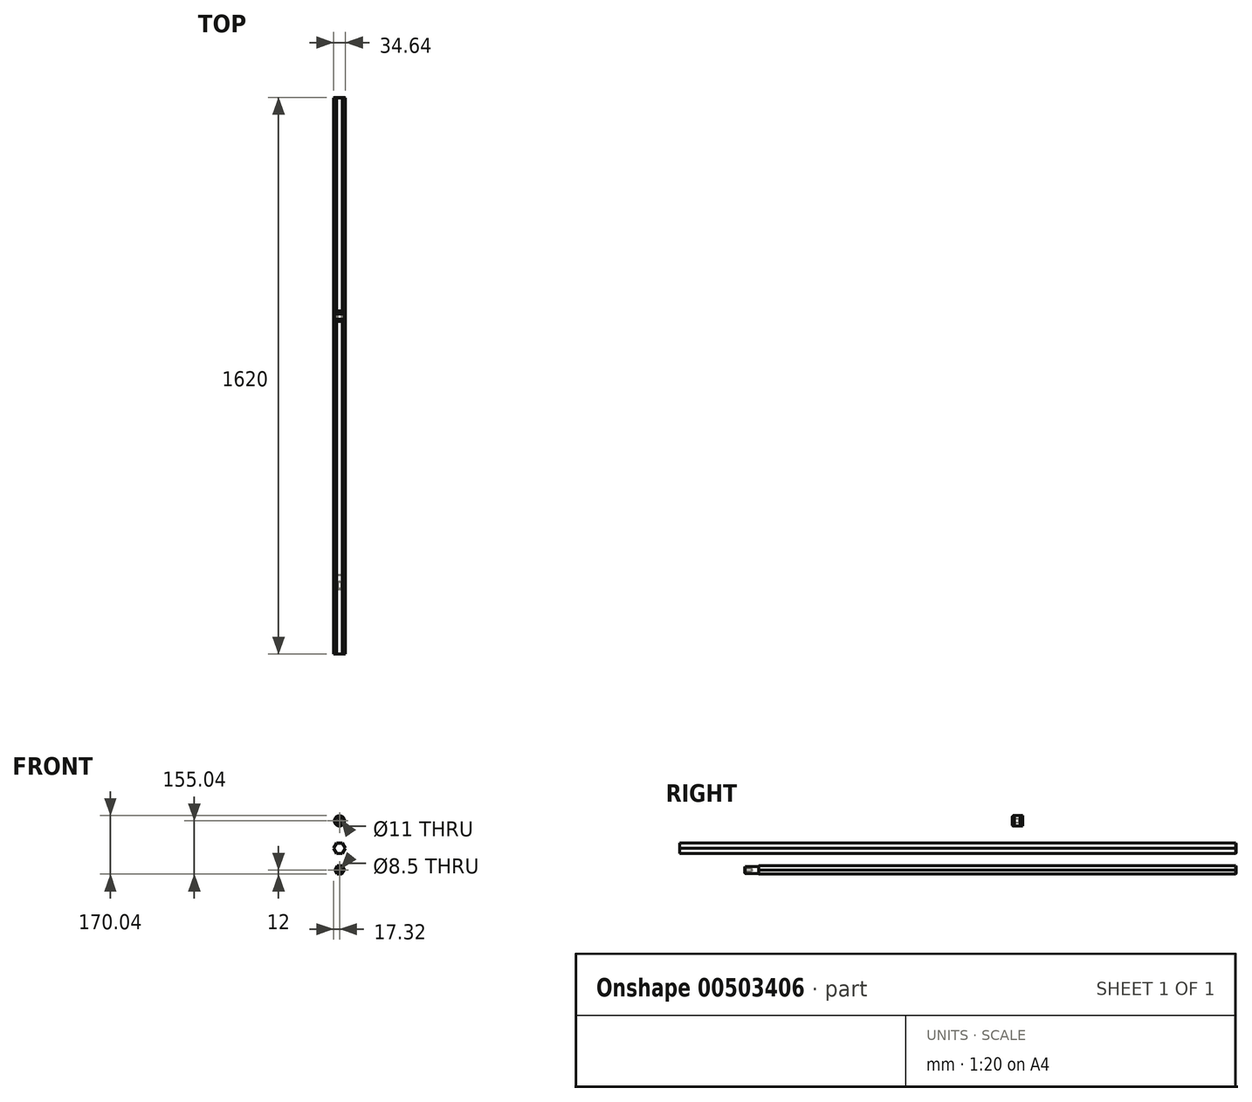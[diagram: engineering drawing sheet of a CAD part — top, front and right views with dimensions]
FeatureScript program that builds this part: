
annotation { "Feature Type Name" : "Feature", "Feature Type Description" : "" }
export const myFeature = defineFeature(function(context is Context, id is Id, definition is map)
    precondition{}
    {
        {
            var Q0;
            Q0=qCreatedBy(makeId("Front.planeOp"),FACE);
            var sketch = newSketch(context, id + "F0", { "sketchPlane" : qUnion([Q0])});
            skCircle(sketch, "E0.cCircle", {"center": v(0, 0) * mm, "radius": 15 * mm, "construction": true});
            skLineSegment(sketch, "E0.0", {"start": v(8.66, -15) * mm, "end": v(-8.66, -15) * mm});
            skLineSegment(sketch, "E0.1", {"start": v(-8.66, -15) * mm, "end": v(-17.32, 0) * mm});
            skLineSegment(sketch, "E0.2", {"start": v(-17.32, 0) * mm, "end": v(-8.66, 15) * mm});
            skLineSegment(sketch, "E0.3", {"start": v(-8.66, 15) * mm, "end": v(8.66, 15) * mm});
            skLineSegment(sketch, "E0.4", {"start": v(8.66, 15) * mm, "end": v(17.32, 0) * mm});
            skLineSegment(sketch, "E0.5", {"start": v(17.32, 0) * mm, "end": v(8.66, -15) * mm});
            skPoint(sketch, "E0.0.midPoint", {"position": v(0, -15) * mm});
            skSolve(sketch);
        }
        {
            var Q0;
            Q0=makeQuery(id+"F0.imprint","IMPRINT",FACE,{"disambiguationData":[TD([[makeQuery(id+"F0.imprint","IMPRINT",EDGE,{"derivedFrom":sQuery(id+"F0.wireOp",EDGE,"E0.0")}),-1.0]])]});
            extrude(context, id + "F1", {"entities" : qUnion([Q0]), "depth" : 1620 * mm});
        }
        {
            var Q0;
            Q0=qCreatedBy(makeId("Right.planeOp"),FACE);
            var sketch = newSketch(context, id + "F2", { "sketchPlane" : qUnion([Q0])});
            skLineSegment(sketch, "E1", {"start": v(-621.45, 0) * mm, "end": v(-621.45, 15) * mm});
            skLineSegment(sketch, "E2", {"start": v(-621.45, 15) * mm, "end": v(-628.45, 15) * mm});
            skLineSegment(sketch, "E3", {"start": v(-628.45, 15) * mm, "end": v(-628.45, 14) * mm});
            skLineSegment(sketch, "E4", {"start": v(-628.45, 14) * mm, "end": v(-629.65, 14) * mm});
            skLineSegment(sketch, "E5", {"start": v(-629.65, 14) * mm, "end": v(-629.65, 15) * mm});
            skLineSegment(sketch, "E6", {"start": v(-629.65, 15) * mm, "end": v(-645.65, 15) * mm});
            skLineSegment(sketch, "E7", {"start": v(-645.65, 15) * mm, "end": v(-645.65, 14) * mm});
            skLineSegment(sketch, "E8", {"start": v(-645.65, 14) * mm, "end": v(-646.85, 14) * mm});
            skLineSegment(sketch, "E9", {"start": v(-646.85, 14) * mm, "end": v(-646.85, 15) * mm});
            skLineSegment(sketch, "E10", {"start": v(-646.85, 15) * mm, "end": v(-651.85, 15) * mm});
            skLineSegment(sketch, "E11", {"start": v(-651.85, 15) * mm, "end": v(-651.85, 0) * mm});
            skLineSegment(sketch, "E12", {"start": v(-651.85, 0) * mm, "end": v(-621.45, 0) * mm});
            skSolve(sketch);
        }
        {
            var Q0;
            Q0=makeQuery(id+"F2.imprint","IMPRINT",FACE,{"disambiguationData":[TD([[makeQuery(id+"F2.imprint","IMPRINT",EDGE,{"derivedFrom":sQuery(id+"F2.wireOp",EDGE,"E1")}),1.0]])]});
            var Q1;
            Q1=sQuery(id+"F2.wireOp",EDGE,"E12");
            revolve(context, id + "F3", {"entities" : qUnion([Q0]), "axis" : qUnion([Q1]), "revolveType" : RevolveType.FULL});
        }
        {
            var Q0;
            Q0=makeQuery(id+"F3.opRevolve","SWEPT_EDGE",EDGE,{"disambiguationData":[OSD([sQuery(id+"F2.wireOp",EDGE,"E10"),sQuery(id+"F2.wireOp",EDGE,"E11")])]});
            chamfer(context, id + "F4", {"entities" : qUnion([Q0]), "width" : 2 * mm, "tangentPropagation" : true});
        }
        {
            var Q0;
            Q0=makeQuery(id+"F3.opRevolve","SWEPT_FACE",FACE,{"disambiguationData":[OSD([sQuery(id+"F2.wireOp",EDGE,"E11")])]});
            var sketch = newSketch(context, id + "F5", { "sketchPlane" : qUnion([Q0])});
            skPoint(sketch, "E13", {"position": v(0, 0) * mm});
            skSolve(sketch);
        }
        {
            var Q0;
            Q0=sQuery(id+"F5.wireOp",VERTEX,"E13");
            var Q1;
            Q1=makeQuery(id+"F3.opRevolve","SWEPT_BODY",BODY,{"disambiguationData":[OSD([sQuery(id+"F2.wireOp",EDGE,"E1"),sQuery(id+"F2.wireOp",EDGE,"E2"),sQuery(id+"F2.wireOp",EDGE,"E3"),sQuery(id+"F2.wireOp",EDGE,"E4"),sQuery(id+"F2.wireOp",EDGE,"E5"),sQuery(id+"F2.wireOp",EDGE,"E6"),sQuery(id+"F2.wireOp",EDGE,"E7"),sQuery(id+"F2.wireOp",EDGE,"E8"),sQuery(id+"F2.wireOp",EDGE,"E9"),sQuery(id+"F2.wireOp",EDGE,"E10"),sQuery(id+"F2.wireOp",EDGE,"E11"),sQuery(id+"F2.wireOp",EDGE,"E12")])]});
            hole(context, id + "F6", {"style" : HoleStyle.SIMPLE, "endStyle" : HoleEndStyle.BLIND, "standardTappedOrClearance" : lookupTablePath({ "standard" : "ISO", "fit" : "Normal", "size" : "M10", "type" : "Clearance" }), "standardBlindInLast" : lookupTablePath({ "fit" : "Standard", "standard" : "ISO", "size" : "M10", "type" : "Clearance" }), "holeDiameter" : 11 * mm, "holeDepth" : 20 * mm, "isTappedThrough" : true, "tappedDepth" : 12 * mm, "tapClearance" : 3, "startFromSketch" : true, "locations" : qUnion([Q0]), "scope" : qUnion([Q1])});
        }
        {
            var Q0;
            Q0=makeQuery(id+"F3.opRevolve","SWEPT_BODY",BODY,{"disambiguationData":[OSD([sQuery(id+"F2.wireOp",EDGE,"E1"),sQuery(id+"F2.wireOp",EDGE,"E2"),sQuery(id+"F2.wireOp",EDGE,"E3"),sQuery(id+"F2.wireOp",EDGE,"E4"),sQuery(id+"F2.wireOp",EDGE,"E5"),sQuery(id+"F2.wireOp",EDGE,"E6"),sQuery(id+"F2.wireOp",EDGE,"E7"),sQuery(id+"F2.wireOp",EDGE,"E8"),sQuery(id+"F2.wireOp",EDGE,"E9"),sQuery(id+"F2.wireOp",EDGE,"E10"),sQuery(id+"F2.wireOp",EDGE,"E11"),sQuery(id+"F2.wireOp",EDGE,"E12")])]});
            transform(context, id + "F7", {"entities" : qUnion([Q0]), "transformType" : TransformType.TRANSLATION_3D, "dx" : 0 * mm, "dy" : 0 * mm, "dz" : 80 * mm, "makeCopy" : false});
        }
        {
            var Q0;
            Q0=makeQuery(id+"F1.opExtrude","CAP_FACE",FACE,{"disambiguationData":[OSD([sQuery(id+"F0.wireOp",EDGE,"E0.0"),sQuery(id+"F0.wireOp",EDGE,"E0.1"),sQuery(id+"F0.wireOp",EDGE,"E0.2"),sQuery(id+"F0.wireOp",EDGE,"E0.3"),sQuery(id+"F0.wireOp",EDGE,"E0.4"),sQuery(id+"F0.wireOp",EDGE,"E0.5")])],"isStart":true});
            chamfer(context, id + "F8", {"entities" : qUnion([Q0]), "width" : 2 * mm, "tangentPropagation" : true});
        }
        {
            var Q0;
            Q0=qCreatedBy(makeId("Front.planeOp"),FACE);
            var sketch = newSketch(context, id + "F9", { "sketchPlane" : qUnion([Q0])});
            skCircle(sketch, "E14.cCircle", {"center": v(0, -63.04) * mm, "radius": 12 * mm, "construction": true});
            skLineSegment(sketch, "E14.0", {"start": v(6.93, -75.04) * mm, "end": v(-6.93, -75.04) * mm});
            skLineSegment(sketch, "E14.1", {"start": v(-6.93, -75.04) * mm, "end": v(-13.86, -63.04) * mm});
            skLineSegment(sketch, "E14.2", {"start": v(-13.86, -63.04) * mm, "end": v(-6.93, -51.04) * mm});
            skLineSegment(sketch, "E14.3", {"start": v(-6.93, -51.04) * mm, "end": v(6.93, -51.04) * mm});
            skLineSegment(sketch, "E14.4", {"start": v(6.93, -51.04) * mm, "end": v(13.86, -63.04) * mm});
            skLineSegment(sketch, "E14.5", {"start": v(13.86, -63.04) * mm, "end": v(6.93, -75.04) * mm});
            skPoint(sketch, "E14.0.midPoint", {"position": v(0, -75.04) * mm});
            skSolve(sketch);
        }
        {
            var Q0;
            Q0=makeQuery(id+"F9.imprint","IMPRINT",FACE,{"disambiguationData":[TD([[makeQuery(id+"F9.imprint","IMPRINT",EDGE,{"derivedFrom":sQuery(id+"F9.wireOp",EDGE,"E14.0")}),-1.0]])]});
            extrude(context, id + "F10", {"entities" : qUnion([Q0]), "depth" : 1390 * mm});
        }
        {
            var Q0;
            Q0=makeQuery(id+"F10.opExtrude","CAP_FACE",FACE,{"disambiguationData":[OSD([sQuery(id+"F9.wireOp",EDGE,"E14.0"),sQuery(id+"F9.wireOp",EDGE,"E14.1"),sQuery(id+"F9.wireOp",EDGE,"E14.2"),sQuery(id+"F9.wireOp",EDGE,"E14.3"),sQuery(id+"F9.wireOp",EDGE,"E14.4"),sQuery(id+"F9.wireOp",EDGE,"E14.5")])],"isStart":false});
            var sketch = newSketch(context, id + "F11", { "sketchPlane" : qUnion([Q0])});
            skCircle(sketch, "E15", {"center": v(0, -63.04) * mm, "radius": 10 * mm});
            skSolve(sketch);
        }
        {
            var Q0;
            Q0=makeQuery(id+"F11.imprint","IMPRINT",FACE,{"disambiguationData":[TD([[makeQuery(id+"F11.imprint","IMPRINT",EDGE,{"derivedFrom":sQuery(id+"F11.wireOp",EDGE,"E15")}),1.0]])]});
            extrude(context, id + "F12", {"entities" : qUnion([Q0]), "operationType" : NewBodyOperationType.ADD, "depth" : 41 * mm});
        }
        {
            var Q0;
            Q0=makeQuery(id+"F12.opExtrude","CAP_EDGE",EDGE,{"disambiguationData":[OSD([sQuery(id+"F11.wireOp",EDGE,"E15")])],"isStart":false});
            chamfer(context, id + "F13", {"entities" : qUnion([Q0]), "width" : 2 * mm, "tangentPropagation" : true});
        }
        {
            var Q0;
            Q0=makeQuery(id+"F10.opExtrude","CAP_FACE",FACE,{"disambiguationData":[OSD([sQuery(id+"F9.wireOp",EDGE,"E14.0"),sQuery(id+"F9.wireOp",EDGE,"E14.1"),sQuery(id+"F9.wireOp",EDGE,"E14.2"),sQuery(id+"F9.wireOp",EDGE,"E14.3"),sQuery(id+"F9.wireOp",EDGE,"E14.4"),sQuery(id+"F9.wireOp",EDGE,"E14.5")])],"isStart":true});
            chamfer(context, id + "F14", {"entities" : qUnion([Q0]), "width" : 2 * mm, "tangentPropagation" : true});
        }
        {
            var Q0;
            Q0=makeQuery(id+"F12.opExtrude","CAP_FACE",FACE,{"disambiguationData":[OSD([sQuery(id+"F11.wireOp",EDGE,"E15")])],"isStart":false});
            var sketch = newSketch(context, id + "F15", { "sketchPlane" : qUnion([Q0])});
            skPoint(sketch, "E16", {"position": v(0, -63.04) * mm});
            skSolve(sketch);
        }
        {
            var Q0;
            Q0=sQuery(id+"F15.wireOp",VERTEX,"E16");
            var Q1;
            Q1=makeQuery(id+"F10.opExtrude","SWEPT_BODY",BODY,{"disambiguationData":[OSD([sQuery(id+"F9.wireOp",EDGE,"E14.0"),sQuery(id+"F9.wireOp",EDGE,"E14.1"),sQuery(id+"F9.wireOp",EDGE,"E14.2"),sQuery(id+"F9.wireOp",EDGE,"E14.3"),sQuery(id+"F9.wireOp",EDGE,"E14.4"),sQuery(id+"F9.wireOp",EDGE,"E14.5")])]});
            hole(context, id + "F16", {"style" : HoleStyle.SIMPLE, "endStyle" : HoleEndStyle.BLIND, "standardTappedOrClearance" : lookupTablePath({ "standard" : "ISO", "engagement" : "75%", "pitch" : "1.5 mm", "size" : "M10", "type" : "Tapped" }), "standardBlindInLast" : lookupTablePath({ "standard" : "ISO", "engagement" : "75%", "pitch" : "1.5 mm", "size" : "M10", "type" : "Tapped" }), "holeDiameter" : 8.5 * mm, "showTappedDepth" : true, "holeDepth" : 20.5 * mm, "isTappedThrough" : true, "tappedDepth" : 16 * mm, "tapClearance" : 3, "startFromSketch" : true, "locations" : qUnion([Q0]), "scope" : qUnion([Q1]), "majorDiameter" : 10 * mm});
        }
    });
